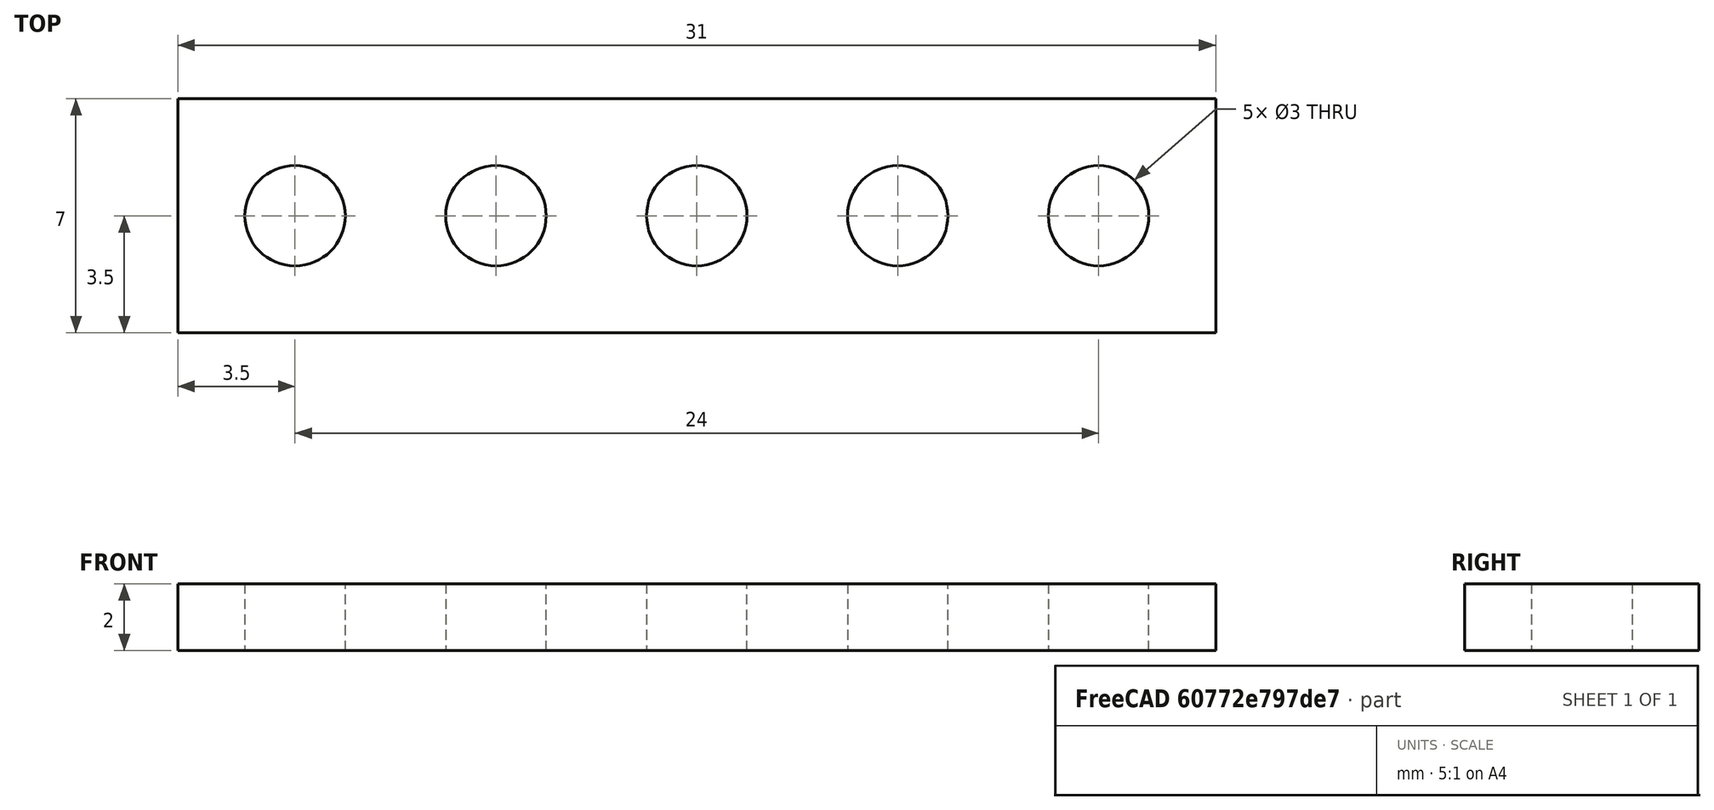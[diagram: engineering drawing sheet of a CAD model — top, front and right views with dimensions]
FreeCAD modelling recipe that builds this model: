
FCSTD DOCUMENT  (FreeCAD 1.0R39319 (Git))
Label: legoraro
License: All rights reserved
LicenseURL: https://en.wikipedia.org/wiki/All_rights_reserved
objects: Part::Box×1, Part::Cylinder×1, Part::FeaturePython×1, Part::Cut×1
note: 4 computed .brp shape members not serialized (recipe doc carries the construction recipe); baked Part::Feature solids carry a one-line shape summary decoded from their .brp

FEATURE [Part::Box] Box  label="Cube"
  AttacherType = Attacher::AttachEngine3D
  Height = 2
  Length = 31
  Width = 7
FEATURE [Part::Cylinder] Cylinder
  Angle = 360
  AttacherType = Attacher::AttachEngine3D
  FirstAngle = 0
  Height = 2
  Placement = pos=(3.5,3.5,0) rot=(0,0,1;0rad)
  Radius = 1.5
  SecondAngle = 0
FEATURE [Part::FeaturePython] Array  # Draft array (typed FeaturePython)
  AlwaysSyncPlacement = false
  Angle = 360
  ArrayType = 0
  Axis = (0,0,1)
  Base = -> Cylinder
  Center = (0,0,0)
  Count = 5
  ExpandArray = false
  Fuse = true
  IntervalAxis = (0,0,0)
  IntervalX = (6,0,0)
  IntervalY = (0,0,0)
  IntervalZ = (0,0,0)
  NumberCircles = 3
  NumberPolar = 5
  NumberX = 5
  NumberY = 1
  NumberZ = 1
  PlacementList = 5 placements: arithmetic series from (3.5,3.5,0) step (6,0,0) to (27.5,3.5,0)
  RadialDistance = 50
  ScaleList = (5) [(1,1,1),(1,1,1),(1,1,1),(1,1,1),(1,1,1)]
  Symmetry = 1
  TangentialDistance = 25
FEATURE [Part::Cut] Cut
  Base = -> Box
  Refine = true
  Tool = -> Array
